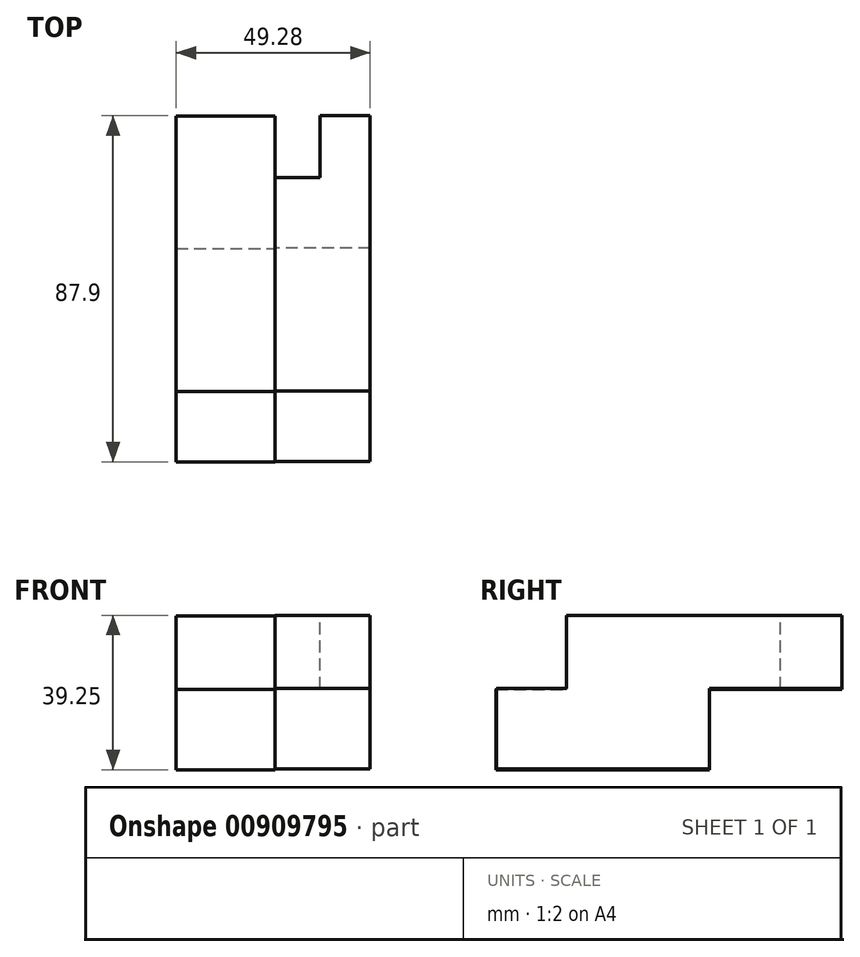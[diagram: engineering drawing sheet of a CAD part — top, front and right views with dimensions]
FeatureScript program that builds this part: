
annotation { "Feature Type Name" : "Feature", "Feature Type Description" : "" }
export const myFeature = defineFeature(function(context is Context, id is Id, definition is map)
    precondition{}
    {
        {
            var Q0;
            Q0=qCreatedBy(makeId("Right.planeOp"),FACE);
            var sketch = newSketch(context, id + "F0", { "sketchPlane" : qUnion([Q0])});
            skLineSegment(sketch, "E0.bottom", {"start": v(-69.96, 21.48) * mm, "end": v(0, 21.48) * mm});
            skLineSegment(sketch, "E0.top", {"start": v(-69.96, 2.86) * mm, "end": v(0, 2.86) * mm});
            skLineSegment(sketch, "E0.left", {"start": v(-69.96, 21.48) * mm, "end": v(-69.96, 2.86) * mm});
            skLineSegment(sketch, "E0.right", {"start": v(0, 21.48) * mm, "end": v(0, 2.86) * mm});
            skLineSegment(sketch, "E1.bottom", {"start": v(-87.85, 2.86) * mm, "end": v(-33.64, 2.86) * mm});
            skLineSegment(sketch, "E1.top", {"start": v(-87.85, -17.6) * mm, "end": v(-33.64, -17.6) * mm});
            skLineSegment(sketch, "E1.left", {"start": v(-87.85, 2.86) * mm, "end": v(-87.85, -17.6) * mm});
            skLineSegment(sketch, "E1.right", {"start": v(-33.64, 2.86) * mm, "end": v(-33.64, -17.6) * mm});
            skSolve(sketch);
        }
        {
            var Q0;
            Q0 = qSketchRegion(id + "F0", true);
            extrude(context, id + "F1", {"entities" : qUnion([Q0]), "depth" : 24.13 * mm, "offsetDistance" : 25.4 * mm});
        }
        {
            var Q0;
            Q0=qCreatedBy(makeId("Right.planeOp"),FACE);
            var sketch = newSketch(context, id + "F2", { "sketchPlane" : qUnion([Q0])});
            skLineSegment(sketch, "E2.bottom", {"start": v(-15.69, 1.94) * mm, "end": v(0, 1.94) * mm});
            skLineSegment(sketch, "E2.top", {"start": v(-15.69, 22.4) * mm, "end": v(0, 22.4) * mm});
            skLineSegment(sketch, "E2.left", {"start": v(-15.69, 1.94) * mm, "end": v(-15.69, 22.4) * mm});
            skLineSegment(sketch, "E2.right", {"start": v(0, 1.94) * mm, "end": v(0, 22.4) * mm});
            skSolve(sketch);
        }
        {
            var Q0;
            Q0 = qSketchRegion(id + "F2", true);
            extrude(context, id + "F3", {"entities" : qUnion([Q0]), "operationType" : NewBodyOperationType.REMOVE, "depth" : 11.43 * mm, "offsetDistance" : 25.4 * mm});
        }
        {
            var Q0;
            Q0=qCreatedBy(makeId("Right.planeOp"),FACE);
            var sketch = newSketch(context, id + "F4", { "sketchPlane" : qUnion([Q0])});
            skLineSegment(sketch, "E3.right", {"start": v(45.55, 186.7) * mm, "end": v(45.55, 168.08) * mm});
            skLineSegment(sketch, "E4.bottom", {"start": v(-70.02, 21.31) * mm, "end": v(-0.06, 21.31) * mm});
            skLineSegment(sketch, "E4.top", {"start": v(-70.02, 2.7) * mm, "end": v(-0.06, 2.7) * mm});
            skLineSegment(sketch, "E4.left", {"start": v(-70.02, 21.31) * mm, "end": v(-70.02, 2.7) * mm});
            skLineSegment(sketch, "E4.right", {"start": v(-0.06, 21.31) * mm, "end": v(-0.06, 2.7) * mm});
            skLineSegment(sketch, "E5.bottom", {"start": v(-87.9, 2.7) * mm, "end": v(-33.7, 2.7) * mm});
            skLineSegment(sketch, "E5.top", {"start": v(-87.9, -17.77) * mm, "end": v(-33.7, -17.77) * mm});
            skLineSegment(sketch, "E5.left", {"start": v(-87.9, 2.7) * mm, "end": v(-87.9, -17.77) * mm});
            skLineSegment(sketch, "E5.right", {"start": v(-33.7, 2.7) * mm, "end": v(-33.7, -17.77) * mm});
            skSolve(sketch);
        }
        {
            var Q0;
            Q0 = qSketchRegion(id + "F4", true);
            extrude(context, id + "F5", {"entities" : qUnion([Q0]), "operationType" : NewBodyOperationType.ADD, "oppositeDirection" : true, "depth" : 25.15 * mm, "offsetDistance" : 25.4 * mm});
        }
    });
